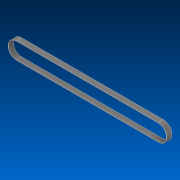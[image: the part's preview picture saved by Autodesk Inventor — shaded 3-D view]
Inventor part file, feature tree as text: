
AUTODESK INVENTOR PART (.ipt)
format: ipt  version: 2022.2 (Build 262287000, 287)  size: 92,160 bytes
history: native  units: in
note: dims shown in document units (in); Inventor stores cm internally (conversion verified against a paired STEP export)
features: extrude x1, sketch x1
ambient origin geometry x8: Origin, YZ Plane, XZ Plane, XY Plane, X Axis, Y Axis, Z Axis, Center Point
bodies: Solid1 (feature_tree)
feature tree (2):
  extrude  "Extrusion1"  Depth=1.128in
  sketch  "Sketch1"  dims[d0=10.0in d1=1.128in d2=0.0394in d3=0.3543in d4=0.0in]
